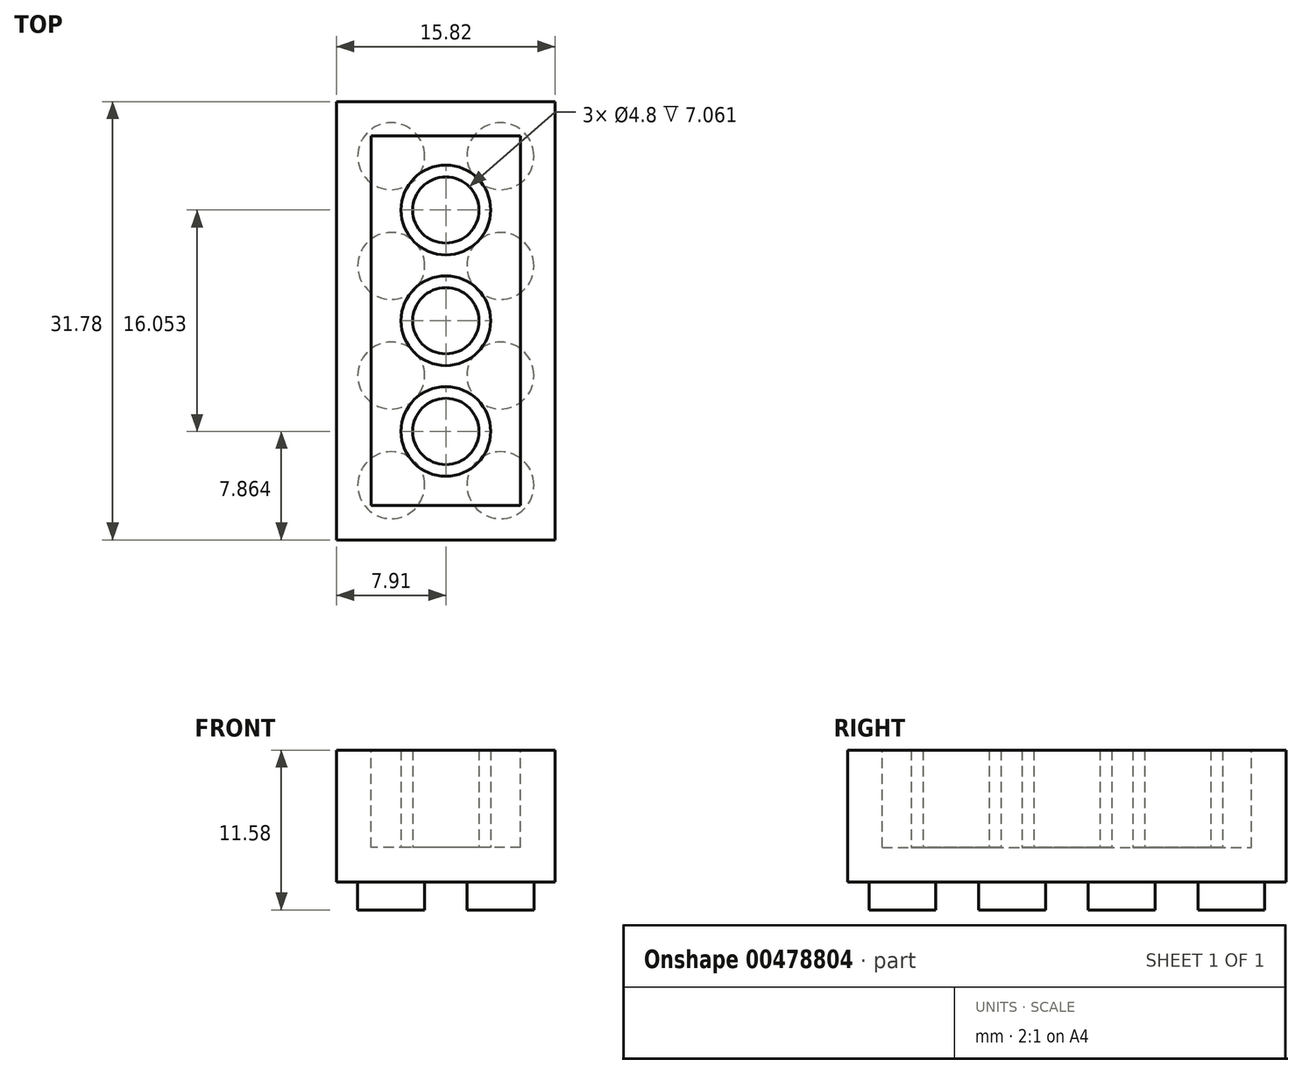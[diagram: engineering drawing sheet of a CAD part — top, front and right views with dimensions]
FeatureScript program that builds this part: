
annotation { "Feature Type Name" : "Feature", "Feature Type Description" : "" }
export const myFeature = defineFeature(function(context is Context, id is Id, definition is map)
    precondition{}
    {
        {
            var Q0;
            Q0=qCreatedBy(makeId("Right.planeOp"),FACE);
            var sketch = newSketch(context, id + "F0", { "sketchPlane" : qUnion([Q0])});
            skLineSegment(sketch, "E0.bottom", {"start": v(0, 0) * mm, "end": v(15.89, 0) * mm});
            skLineSegment(sketch, "E0.top", {"start": v(0, 9.55) * mm, "end": v(15.89, 9.55) * mm});
            skLineSegment(sketch, "E0.left", {"start": v(0, 0) * mm, "end": v(0, 9.55) * mm});
            skLineSegment(sketch, "E0.right", {"start": v(15.89, 0) * mm, "end": v(15.89, 9.55) * mm});
            skSolve(sketch);
        }
        {
            var Q0;
            Q0=makeQuery(id+"F0.imprint","IMPRINT",FACE,{"disambiguationData":[TD([[makeQuery(id+"F0.imprint","IMPRINT",EDGE,{"derivedFrom":sQuery(id+"F0.wireOp",EDGE,"E0.bottom")}),1.0]])]});
            extrude(context, id + "F1", {"entities" : qUnion([Q0]), "depth" : 7.9 * mm});
        }
        {
            var Q0;
            Q0=qCreatedBy(makeId("Top.planeOp"),FACE);
            var sketch = newSketch(context, id + "F2", { "sketchPlane" : qUnion([Q0])});
            skCircle(sketch, "E1", {"center": v(3.96, 3.98) * mm, "radius": 2.43 * mm});
            skCircle(sketch, "E2", {"center": v(3.96, 11.93) * mm, "radius": 2.43 * mm});
            skSolve(sketch);
        }
        {
            var Q0;
            Q0=qSketchRegion(id+"F2",true);
            extrude(context, id + "F3", {"entities" : qUnion([Q0]), "operationType" : NewBodyOperationType.ADD, "oppositeDirection" : true, "depth" : 2.03 * mm});
        }
        {
            var Q0;
            Q0=makeQuery(id+"F1.opExtrude","SWEPT_BODY",BODY,{"disambiguationData":[OSD([sQuery(id+"F0.wireOp",EDGE,"E0.bottom"),sQuery(id+"F0.wireOp",EDGE,"E0.top"),sQuery(id+"F0.wireOp",EDGE,"E0.left"),sQuery(id+"F0.wireOp",EDGE,"E0.right")])]});
            var Q1;
            Q1=qCreatedBy(makeId("Front.planeOp"),FACE);
            mirror(context, id + "F4", {"operationType" : NewBodyOperationType.ADD, "entities" : qUnion([Q0]), "mirrorPlane" : qUnion([Q1])});
        }
        {
            var Q0;
            Q0=makeQuery(id+"F1.opExtrude","SWEPT_BODY",BODY,{"disambiguationData":[OSD([sQuery(id+"F0.wireOp",EDGE,"E0.bottom"),sQuery(id+"F0.wireOp",EDGE,"E0.top"),sQuery(id+"F0.wireOp",EDGE,"E0.left"),sQuery(id+"F0.wireOp",EDGE,"E0.right")])]});
            var Q1;
            Q1=qCreatedBy(makeId("Right.planeOp"),FACE);
            mirror(context, id + "F5", {"operationType" : NewBodyOperationType.ADD, "entities" : qUnion([Q0]), "mirrorPlane" : qUnion([Q1])});
        }
        {
            var Q0;
            {var subQ0=makeQuery(id+"F1.opExtrude","SWEPT_FACE",FACE,{"disambiguationData":[OSD([sQuery(id+"F0.wireOp",EDGE,"E0.top")])]});var subQ1=makeQuery(id+"F4.boolean.opBoolean","MERGE",FACE,{"derivedFrom":[subQ0,makeQuery(id+"F4.opPattern","COPY",FACE,{"derivedFrom":subQ0,"instanceName":"1"})]});Q0=makeQuery(id+"F5.boolean.opBoolean","MERGE",FACE,{"derivedFrom":[subQ1,makeQuery(id+"F5.opPattern","COPY",FACE,{"derivedFrom":subQ1,"instanceName":"1"})]});}
            shell(context, id + "F6", {"entities" : qUnion([Q0]), "thickness" : 2.5 * mm});
        }
        {
            var Q0;
            Q0=makeQuery(id+"F6.opShell","OFFSET_FACE",FACE,{"disambiguationData":[OSD([sQuery(id+"F0.wireOp",EDGE,"E0.bottom")])]});
            var sketch = newSketch(context, id + "F7", { "sketchPlane" : qUnion([Q0])});
            skCircle(sketch, "E3", {"center": v(0, 0) * mm, "radius": 2.4 * mm});
            skCircle(sketch, "E4", {"center": v(0, 8.03) * mm, "radius": 2.4 * mm});
            skCircle(sketch, "E5", {"center": v(0, -8.03) * mm, "radius": 2.4 * mm});
            skCircle(sketch, "E6", {"center": v(0, -8.03) * mm, "radius": 3.25 * mm});
            skCircle(sketch, "E7", {"center": v(0, 0) * mm, "radius": 3.25 * mm});
            skCircle(sketch, "E8", {"center": v(0, 8.03) * mm, "radius": 3.25 * mm});
            skSolve(sketch);
        }
        {
            var Q0;
            Q0=makeQuery(id+"F7.imprint","IMPRINT",FACE,{"disambiguationData":[TD([[makeQuery(id+"F7.imprint","IMPRINT",EDGE,{"derivedFrom":sQuery(id+"F7.wireOp",EDGE,"E5")}),-1.0]])]});
            var Q1;
            Q1=makeQuery(id+"F7.imprint","IMPRINT",FACE,{"disambiguationData":[TD([[makeQuery(id+"F7.imprint","IMPRINT",EDGE,{"derivedFrom":sQuery(id+"F7.wireOp",EDGE,"E3")}),-1.0]])]});
            var Q2;
            Q2=makeQuery(id+"F7.imprint","IMPRINT",FACE,{"disambiguationData":[TD([[makeQuery(id+"F7.imprint","IMPRINT",EDGE,{"derivedFrom":sQuery(id+"F7.wireOp",EDGE,"E4")}),-1.0]])]});
            var Q3;
            {var subQ0=makeQuery(id+"F1.opExtrude","SWEPT_FACE",FACE,{"disambiguationData":[OSD([sQuery(id+"F0.wireOp",EDGE,"E0.top")])]});var subQ1=makeQuery(id+"F4.boolean.opBoolean","MERGE",FACE,{"derivedFrom":[subQ0,makeQuery(id+"F4.opPattern","COPY",FACE,{"derivedFrom":subQ0,"instanceName":"1"})]});Q3=makeQuery(id+"F5.boolean.opBoolean","MERGE",FACE,{"derivedFrom":[subQ1,makeQuery(id+"F5.opPattern","COPY",FACE,{"derivedFrom":subQ1,"instanceName":"1"})]});}
            extrude(context, id + "F8", {"entities" : qUnion([Q0, Q1, Q2]), "operationType" : NewBodyOperationType.ADD, "endBound" : BoundingType.UP_TO_SURFACE, "endBoundEntityFace" : qUnion([Q3]), "depth" : 25.4 * mm});
        }
    });
